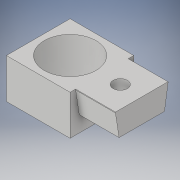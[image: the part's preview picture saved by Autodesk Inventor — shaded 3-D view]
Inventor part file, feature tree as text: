
AUTODESK INVENTOR PART (.ipt)
format: ipt  version: 2018 (Build 220112000, 112)  size: 133,632 bytes
history: native  units: in
note: dims shown in document units (in); Inventor stores cm internally (conversion verified against a paired STEP export)
features: extrude x4, sketch x4, projected_geometry x1
ambient origin geometry x8: Origin, YZ Plane, XZ Plane, XY Plane, X Axis, Y Axis, Z Axis, Center Point
bodies: Solid1 (feature_tree)
feature tree (9):
  extrude  "Extrusion1"  Depth=0.8in
  extrude  "Extrusion2"  Depth=0.4in
  extrude  "Extrusion3"  Depth=0.5in TaperAngle=0.0deg
  extrude  "Extrusion4"  Depth=0.5in
  sketch  "Sketch1"  dims[d0=0.8in d1=0.8in]
  sketch  "Sketch2"  dims[d2=0.4in d3=0.4in]
  sketch  "Sketch3"  dims[d4=0.65in d5=0.5in d6=0.0in]
  sketch  "Sketch4"  dims[d7=0.66in d8=0.57in d9=0.29in d10=0.2in d11=0.115in d12=0.5in d13=0.0in d14=0.18in d15=0.27in d16=0.7in d17=0.0in d18=1.0in d19=0.0in]
  projected_geometry  "Projected Loop1"
